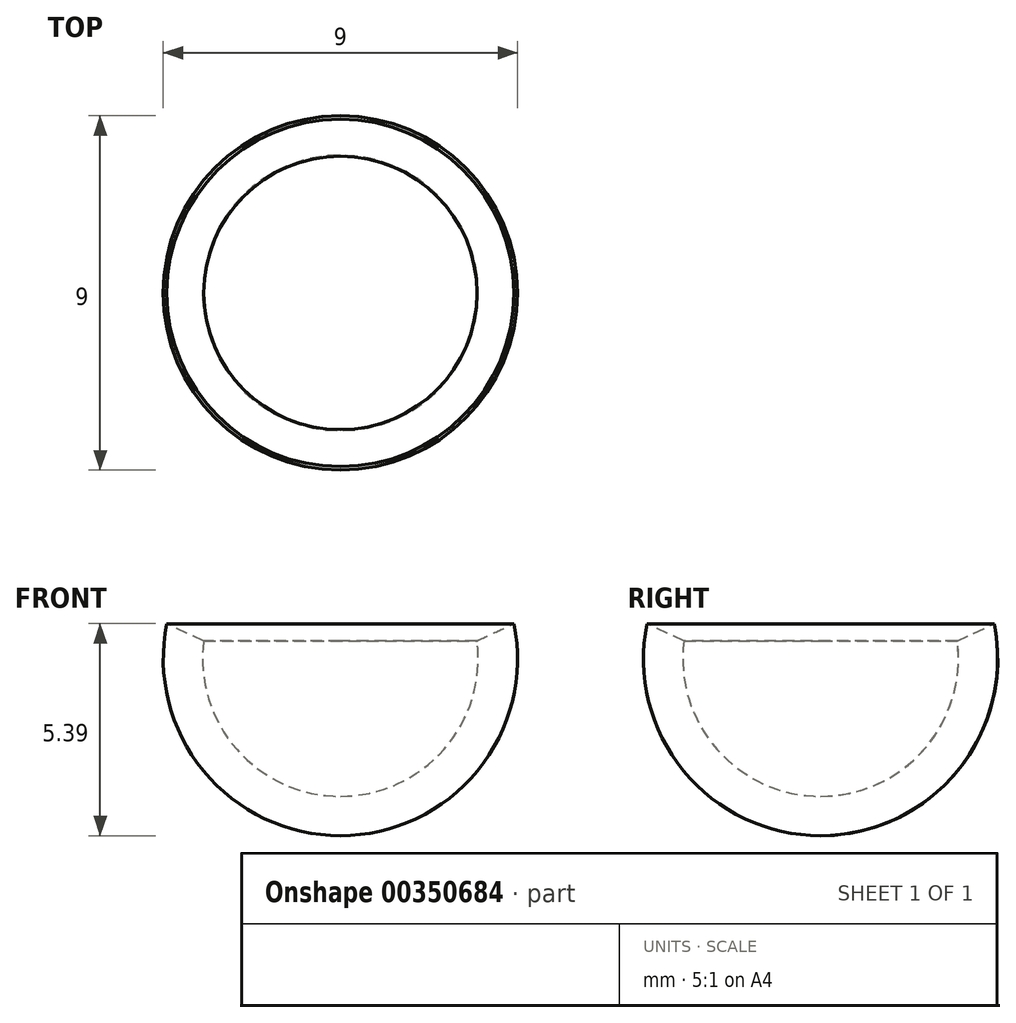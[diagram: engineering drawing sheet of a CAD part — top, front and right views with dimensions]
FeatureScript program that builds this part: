
annotation { "Feature Type Name" : "Feature", "Feature Type Description" : "" }
export const myFeature = defineFeature(function(context is Context, id is Id, definition is map)
    precondition{}
    {
        {
            var Q0;
            Q0=qCreatedBy(makeId("Right.planeOp"),FACE);
            var sketch = newSketch(context, id + "F0", { "sketchPlane" : qUnion([Q0])});
            skArc(sketch, "E0", {"start": v(0, -3.5) * mm, "mid": v(2.63, -2.31) * mm, "end": v(3.47, 0.45) * mm});
            skLineSegment(sketch, "E1", {"start": v(7.38, 0.45) * mm, "end": v(-13.16, 0.45) * mm, "construction": true});
            skLineSegment(sketch, "E2", {"start": v(0, 9.97) * mm, "end": v(0, -13.71) * mm, "construction": true});
            skPoint(sketch, "E2.endSnap0", {"position": v(0, -7.1) * mm});
            skLineSegment(sketch, "E3", {"start": v(4.27, 0.45) * mm, "end": v(3.47, 0.45) * mm});
            skArc(sketch, "E4.0", {"start": v(0, -4.5) * mm, "mid": v(3.48, -2.85) * mm, "end": v(4.41, 0.89) * mm});
            skLineSegment(sketch, "E5", {"start": v(4.41, 0.89) * mm, "end": v(3.47, 0.45) * mm});
            skLineSegment(sketch, "E6", {"start": v(0, -3.5) * mm, "end": v(0, -7.1) * mm});
            skSolve(sketch);
        }
        {
            var Q0;
            Q0 = qSketchRegion(id + "F0", true);
            var Q1;
            Q1=sQuery(id+"F0.wireOp",EDGE,"E2");
            revolve(context, id + "F1", {"entities" : qUnion([Q0]), "axis" : qUnion([Q1]), "revolveType" : RevolveType.FULL});
        }
    });
